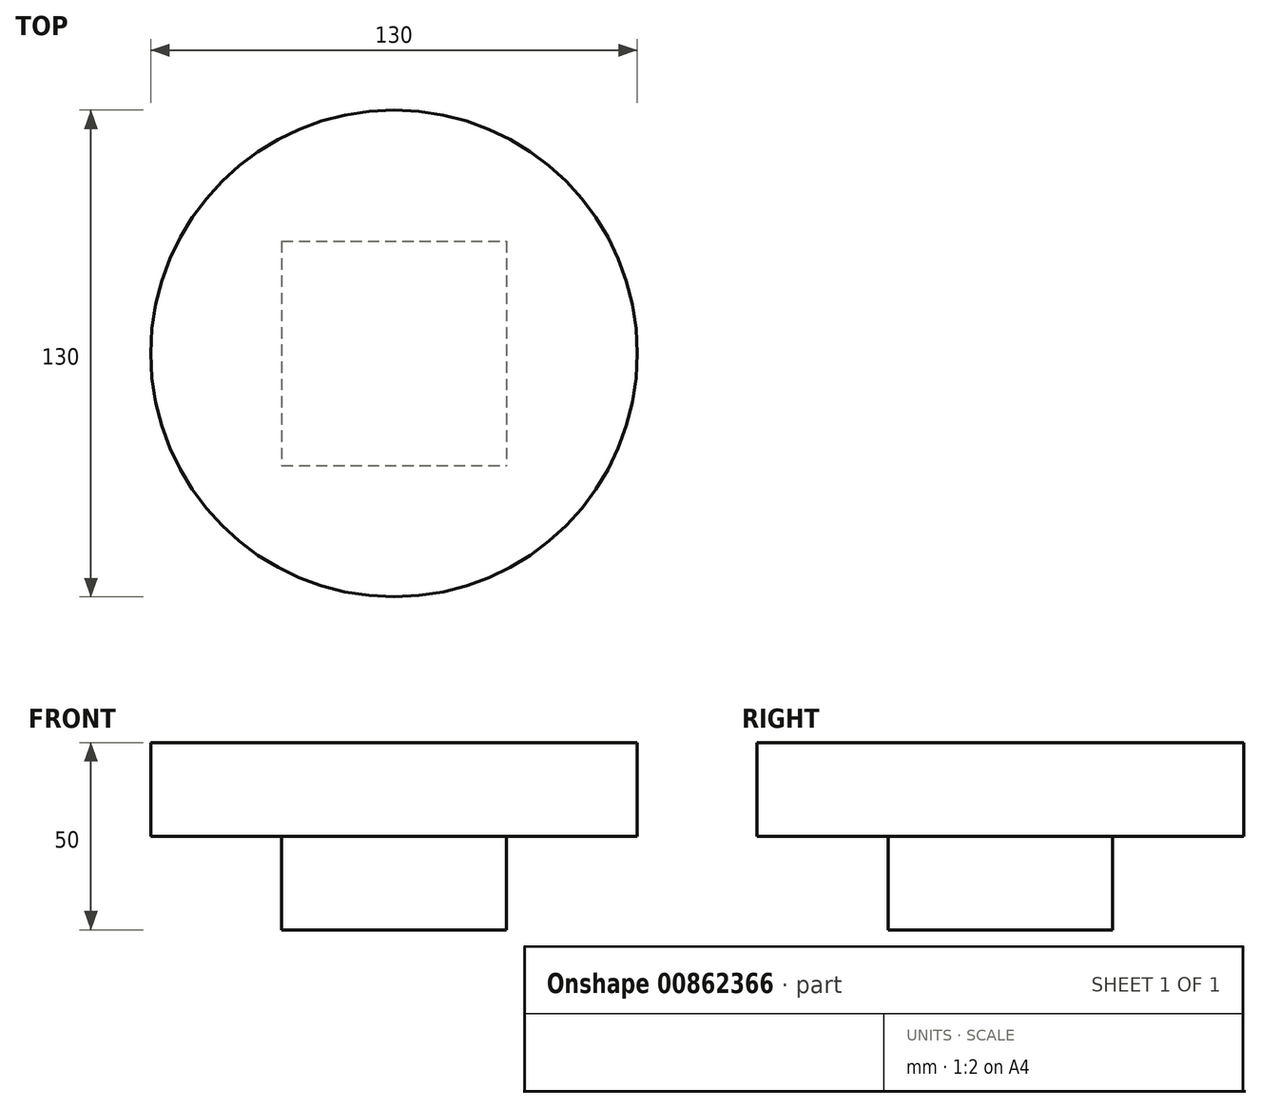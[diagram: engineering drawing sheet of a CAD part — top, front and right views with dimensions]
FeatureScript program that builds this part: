
annotation { "Feature Type Name" : "Feature", "Feature Type Description" : "" }
export const myFeature = defineFeature(function(context is Context, id is Id, definition is map)
    precondition{}
    {
        {
            var Q0;
            Q0=qCreatedBy(makeId("Top.planeOp"),FACE);
            var sketch = newSketch(context, id + "F0", { "sketchPlane" : qUnion([Q0])});
            skLineSegment(sketch, "E0.bottom", {"start": v(-30, 30) * mm, "end": v(30, 30) * mm});
            skLineSegment(sketch, "E0.top", {"start": v(-30, -30) * mm, "end": v(30, -30) * mm});
            skLineSegment(sketch, "E0.left", {"start": v(-30, 30) * mm, "end": v(-30, -30) * mm});
            skLineSegment(sketch, "E0.right", {"start": v(30, 30) * mm, "end": v(30, -30) * mm});
            skPoint(sketch, "E0.middle", {"position": v(0, 0) * mm});
            skSolve(sketch);
        }
        {
            var Q0;
            Q0=makeQuery(id+"F0.imprint","IMPRINT",FACE,{"disambiguationData":[TD([[makeQuery(id+"F0.imprint","IMPRINT",EDGE,{"derivedFrom":sQuery(id+"F0.wireOp",EDGE,"E0.bottom")}),-1.0]])]});
            extrude(context, id + "F1", {"entities" : qUnion([Q0]), "depth" : 25 * mm, "offsetDistance" : 25 * mm});
        }
        {
            var Q0;
            Q0=makeQuery(id+"F1.opExtrude","CAP_FACE",FACE,{"disambiguationData":[OSD([sQuery(id+"F0.wireOp",EDGE,"E0.bottom"),sQuery(id+"F0.wireOp",EDGE,"E0.top"),sQuery(id+"F0.wireOp",EDGE,"E0.left"),sQuery(id+"F0.wireOp",EDGE,"E0.right")])],"isStart":false});
            var sketch = newSketch(context, id + "F2", { "sketchPlane" : qUnion([Q0])});
            skCircle(sketch, "E1", {"center": v(0, 0) * mm, "radius": 65 * mm});
            skSolve(sketch);
        }
        {
            var Q0;
            Q0=makeQuery(id+"F2.imprint","IMPRINT",FACE,{"disambiguationData":[TD([[makeQuery(id+"F2.imprint","IMPRINT",EDGE,{"derivedFrom":makeQuery(id+"F1.opExtrude","CAP_EDGE",EDGE,{"disambiguationData":[OSD([sQuery(id+"F0.wireOp",EDGE,"E0.bottom")])],"isStart":false})}),-1.0]])]});
            var Q1;
            Q1=makeQuery(id+"F2.imprint","IMPRINT",FACE,{"disambiguationData":[TD([[makeQuery(id+"F2.imprint","IMPRINT",EDGE,{"derivedFrom":sQuery(id+"F2.wireOp",EDGE,"E1")}),1.0]])]});
            var Q2;
            Q2=sQuery(id+"F2.wireOp",EDGE,"E1");
            extrude(context, id + "F3", {"entities" : qUnion([Q0, Q1]), "operationType" : NewBodyOperationType.ADD, "surfaceEntities" : qUnion([Q2]), "depth" : 25 * mm, "offsetDistance" : 25 * mm});
        }
    });
